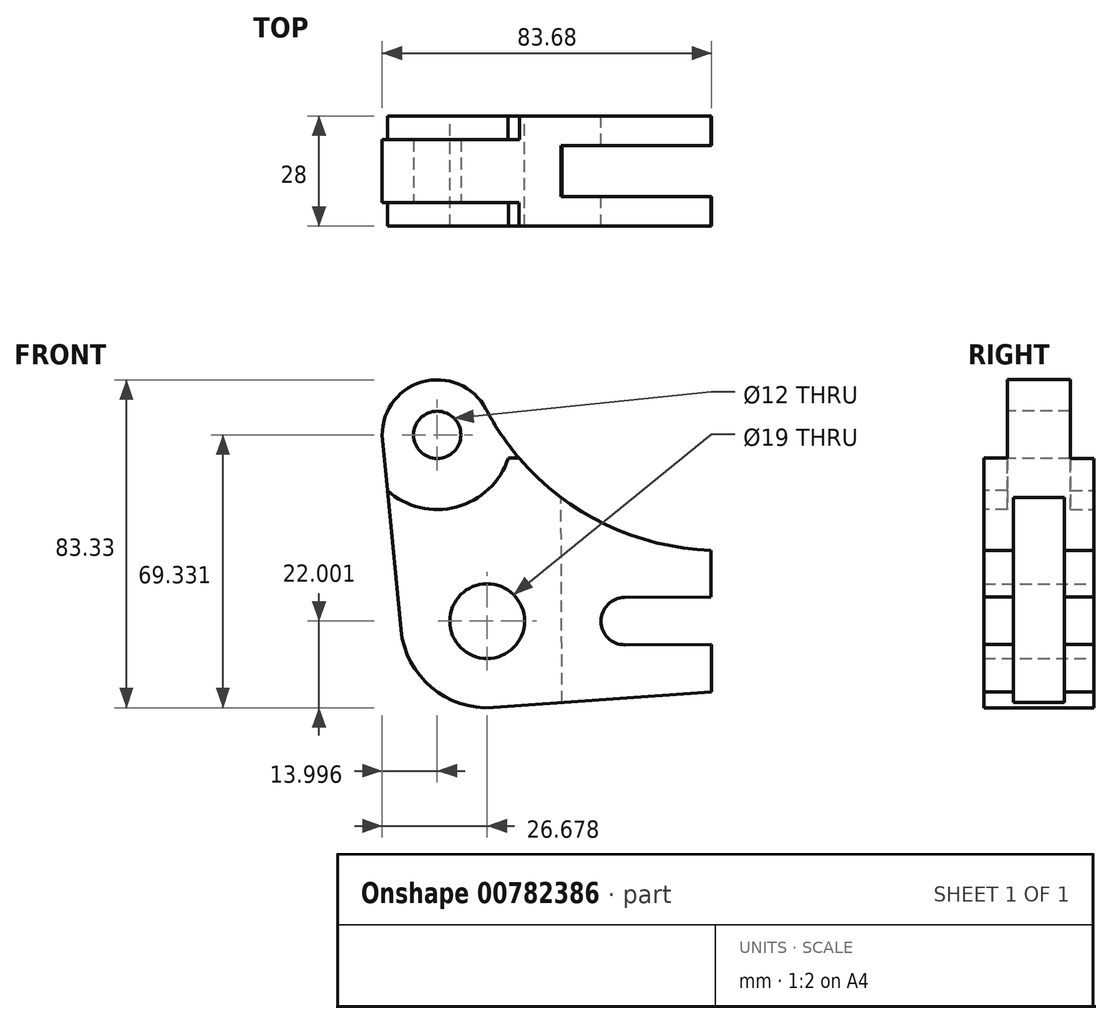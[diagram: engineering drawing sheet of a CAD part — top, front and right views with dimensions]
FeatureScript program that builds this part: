
annotation { "Feature Type Name" : "Feature", "Feature Type Description" : "" }
export const myFeature = defineFeature(function(context is Context, id is Id, definition is map)
    precondition{}
    {
        {
            var Q0;
            Q0=qCreatedBy(makeId("Front.planeOp"),FACE);
            var sketch = newSketch(context, id + "F0", { "sketchPlane" : qUnion([Q0])});
            skLineSegment(sketch, "E0.right", {"start": v(55.28, -7.58) * mm, "end": v(55.33, -19.48) * mm});
            skPoint(sketch, "E0.middle", {"position": v(0, 0) * mm});
            skPoint(sketch, "E1.visualSharp", {"position": v(-55.07, -39.15) * mm});
            skArc(sketch, "E2", {"start": v(-1.85, 28.26) * mm, "mid": v(21.88, 2.63) * mm, "end": v(55.28, -7.58) * mm});
            skArc(sketch, "E3", {"start": v(-1.85, 28.26) * mm, "mid": v(-18.25, 35.16) * mm, "end": v(-28.18, 20.38) * mm});
            skPoint(sketch, "E4.orphan", {"position": v(-55.44, 43.58) * mm});
            skPoint(sketch, "E5.orphan", {"position": v(55.07, 39.15) * mm});
            skPoint(sketch, "E1.filletArc.center.orphan", {"position": v(-1.56, -25.58) * mm});
            skLineSegment(sketch, "E6", {"start": v(-28.18, 20.38) * mm, "end": v(-23.46, -27.73) * mm});
            skArc(sketch, "E7", {"start": v(-23.46, -27.73) * mm, "mid": v(-15.75, -42.4) * mm, "end": v(0, -47.52) * mm});
            skLineSegment(sketch, "E8", {"start": v(55.44, -43.58) * mm, "end": v(0, -47.52) * mm});
            skCircle(sketch, "E9", {"center": v(-1.56, -25.58) * mm, "radius": 9.5 * mm});
            skArc(sketch, "E10", {"start": v(33.33, -19.58) * mm, "mid": v(27.36, -25.6) * mm, "end": v(33.38, -31.58) * mm});
            skLineSegment(sketch, "E11", {"start": v(33.33, -19.58) * mm, "end": v(55.33, -19.48) * mm});
            skLineSegment(sketch, "E12", {"start": v(33.38, -31.58) * mm, "end": v(55.38, -31.48) * mm});
            skLineSegment(sketch, "E13.trimOffspring", {"start": v(55.38, -31.48) * mm, "end": v(55.44, -43.58) * mm});
            skSolve(sketch);
        }
        {
            var Q0;
            Q0=qSketchRegion(id+"F0",true);
            extrude(context, id + "F1", {"entities" : qUnion([Q0]), "depth" : 28 * mm, "offsetDistance" : 25.4 * mm});
        }
        {
            var Q0;
            Q0=makeQuery(id+"F1.opExtrude","CAP_FACE",FACE,{"disambiguationData":[OSD([sQuery(id+"F0.wireOp",EDGE,"E0.right"),sQuery(id+"F0.wireOp",EDGE,"E2"),sQuery(id+"F0.wireOp",EDGE,"E3"),sQuery(id+"F0.wireOp",EDGE,"E6"),sQuery(id+"F0.wireOp",EDGE,"E7"),sQuery(id+"F0.wireOp",EDGE,"E8"),sQuery(id+"F0.wireOp",EDGE,"E9"),sQuery(id+"F0.wireOp",EDGE,"E10"),sQuery(id+"F0.wireOp",EDGE,"E11"),sQuery(id+"F0.wireOp",EDGE,"E12"),sQuery(id+"F0.wireOp",EDGE,"E13.trimOffspring")])],"isStart":false});
            var sketch = newSketch(context, id + "F2", { "sketchPlane" : qUnion([Q0])});
            skCircle(sketch, "E14", {"center": v(-14.24, 21.75) * mm, "radius": 19 * mm});
            skLineSegment(sketch, "E15", {"start": v(-3.02, 15.8) * mm, "end": v(21.66, 15.91) * mm});
            skSolve(sketch);
        }
        {
            var Q0;
            {var subQ5=makeQuery(id+"F1.opExtrude","CAP_EDGE",EDGE,{"disambiguationData":[OSD([sQuery(id+"F0.wireOp",EDGE,"E3")])],"isStart":false});Q0=makeQuery(id+"F2.imprint","IMPRINT",FACE,{"disambiguationData":[TD([[makeQuery(id+"F2.imprint","IMPRINT",EDGE,{"derivedFrom":subQ5}),-1.0]])]});}
            var Q1;
            {var subQ0=sQuery(id+"F2.wireOp",EDGE,"E15");var subQ1=sQuery(id+"F2.wireOp",EDGE,"E14");var subQ2=makeQuery(id+"F2.imprint","INTERSECT",VERTEX,{"derivedFrom":[subQ1,subQ0]});Q1=makeQuery(id+"F2.imprint","IMPRINT",FACE,{"disambiguationData":[TD([[makeQuery(id+"F2.imprint","IMPRINT",EDGE,{"disambiguationData":[TD([[subQ2,-1.0]])],"derivedFrom":subQ1}),-1.0]])]});}
            var Q2;
            {var subQ0=makeQuery(id+"F1.opExtrude","CAP_EDGE",EDGE,{"disambiguationData":[OSD([sQuery(id+"F0.wireOp",EDGE,"E3")])],"isStart":false});Q2=makeQuery(id+"F2.imprint","IMPRINT",FACE,{"disambiguationData":[TD([[makeQuery(id+"F2.imprint","IMPRINT",EDGE,{"derivedFrom":subQ0}),1.0]])]});}
            extrude(context, id + "F3", {"entities" : qUnion([Q0, Q1, Q2]), "operationType" : NewBodyOperationType.REMOVE, "oppositeDirection" : true, "depth" : 6 * mm, "offsetDistance" : 25.4 * mm});
        }
        {
            var Q0;
            Q0=makeQuery(id+"F3.boolean.opBoolean","COPY",FACE,{"derivedFrom":makeQuery(id+"F3.opExtrude","CAP_FACE",FACE,{"disambiguationData":[OSD([sQuery(id+"F2.wireOp",EDGE,"E14")])],"isStart":false})});
            var sketch = newSketch(context, id + "F4", { "sketchPlane" : qUnion([Q0])});
            skSolve(sketch);
        }
        {
            var Q0;
            {var subQ0=sQuery(id+"F2.wireOp",EDGE,"E14");Q0=makeQuery(id+"F4.imprint","IMPRINT",FACE,{"disambiguationData":[TD([[makeQuery(id+"F4.imprint","IMPRINT",EDGE,{"derivedFrom":makeQuery(id+"F3.boolean.opBoolean","COPY",EDGE,{"derivedFrom":makeQuery(id+"F3.opExtrude","CAP_EDGE",EDGE,{"disambiguationData":[OSD([subQ0])],"isStart":false})})}),1.0]])]});}
            var sketch = newSketch(context, id + "F5", { "sketchPlane" : qUnion([Q0])});
            skCircle(sketch, "E16", {"center": v(-14.24, 21.75) * mm, "radius": 6 * mm});
            skSolve(sketch);
        }
        {
            var Q0;
            Q0=qSketchRegion(id+"F5",true);
            extrude(context, id + "F6", {"entities" : qUnion([Q0]), "operationType" : NewBodyOperationType.REMOVE, "endBound" : BoundingType.THROUGH_ALL, "oppositeDirection" : true, "depth" : 25.4 * mm, "offsetDistance" : 25.4 * mm});
        }
        {
            var Q0;
            Q0=makeQuery(id+"F1.opExtrude","SWEPT_FACE",FACE,{"disambiguationData":[OSD([sQuery(id+"F0.wireOp",EDGE,"E0.right")])]});
            var sketch = newSketch(context, id + "F7", { "sketchPlane" : qUnion([Q0])});
            skLineSegment(sketch, "E17.bottom", {"start": v(-7.5, -54.53) * mm, "end": v(-20.5, -54.53) * mm});
            skLineSegment(sketch, "E17.top", {"start": v(-7.5, 9.27) * mm, "end": v(-20.5, 9.27) * mm});
            skLineSegment(sketch, "E17.left", {"start": v(-7.5, -54.53) * mm, "end": v(-7.5, 9.27) * mm});
            skLineSegment(sketch, "E17.right", {"start": v(-20.5, -54.53) * mm, "end": v(-20.5, 9.27) * mm});
            skSolve(sketch);
        }
        {
            var Q0;
            Q0=qSketchRegion(id+"F7",true);
            extrude(context, id + "F8", {"entities" : qUnion([Q0]), "operationType" : NewBodyOperationType.REMOVE, "oppositeDirection" : true, "depth" : 38 * mm, "offsetDistance" : 25.4 * mm});
        }
        {
            var Q0;
            Q0=makeQuery(id+"F1.opExtrude","CAP_FACE",FACE,{"disambiguationData":[OSD([sQuery(id+"F0.wireOp",EDGE,"E0.right"),sQuery(id+"F0.wireOp",EDGE,"E2"),sQuery(id+"F0.wireOp",EDGE,"E3"),sQuery(id+"F0.wireOp",EDGE,"E6"),sQuery(id+"F0.wireOp",EDGE,"E7"),sQuery(id+"F0.wireOp",EDGE,"E8"),sQuery(id+"F0.wireOp",EDGE,"E9"),sQuery(id+"F0.wireOp",EDGE,"E10"),sQuery(id+"F0.wireOp",EDGE,"E11"),sQuery(id+"F0.wireOp",EDGE,"E12"),sQuery(id+"F0.wireOp",EDGE,"E13.trimOffspring")])],"isStart":true});
            var sketch = newSketch(context, id + "F9", { "sketchPlane" : qUnion([Q0])});
            skCircle(sketch, "E18", {"center": v(14.24, 21.75) * mm, "radius": 19 * mm});
            skLineSegment(sketch, "E19", {"start": v(-55.05, 15.75) * mm, "end": v(-3.78, 15.75) * mm});
            skSolve(sketch);
        }
        {
            var Q0;
            Q0=qSketchRegion(id+"F9",true);
            var Q1;
            {var subQ0=sQuery(id+"F9.wireOp",EDGE,"E19");var subQ1=sQuery(id+"F9.wireOp",EDGE,"E18");var subQ2=makeQuery(id+"F9.imprint","INTERSECT",VERTEX,{"derivedFrom":[subQ1,subQ0]});Q1=makeQuery(id+"F9.imprint","IMPRINT",FACE,{"disambiguationData":[TD([[makeQuery(id+"F9.imprint","IMPRINT",EDGE,{"disambiguationData":[TD([[subQ2,1.0]])],"derivedFrom":subQ1}),-1.0]])]});}
            extrude(context, id + "F10", {"entities" : qUnion([Q0, Q1]), "operationType" : NewBodyOperationType.REMOVE, "oppositeDirection" : true, "depth" : 6 * mm, "offsetDistance" : 25.4 * mm});
        }
    });
